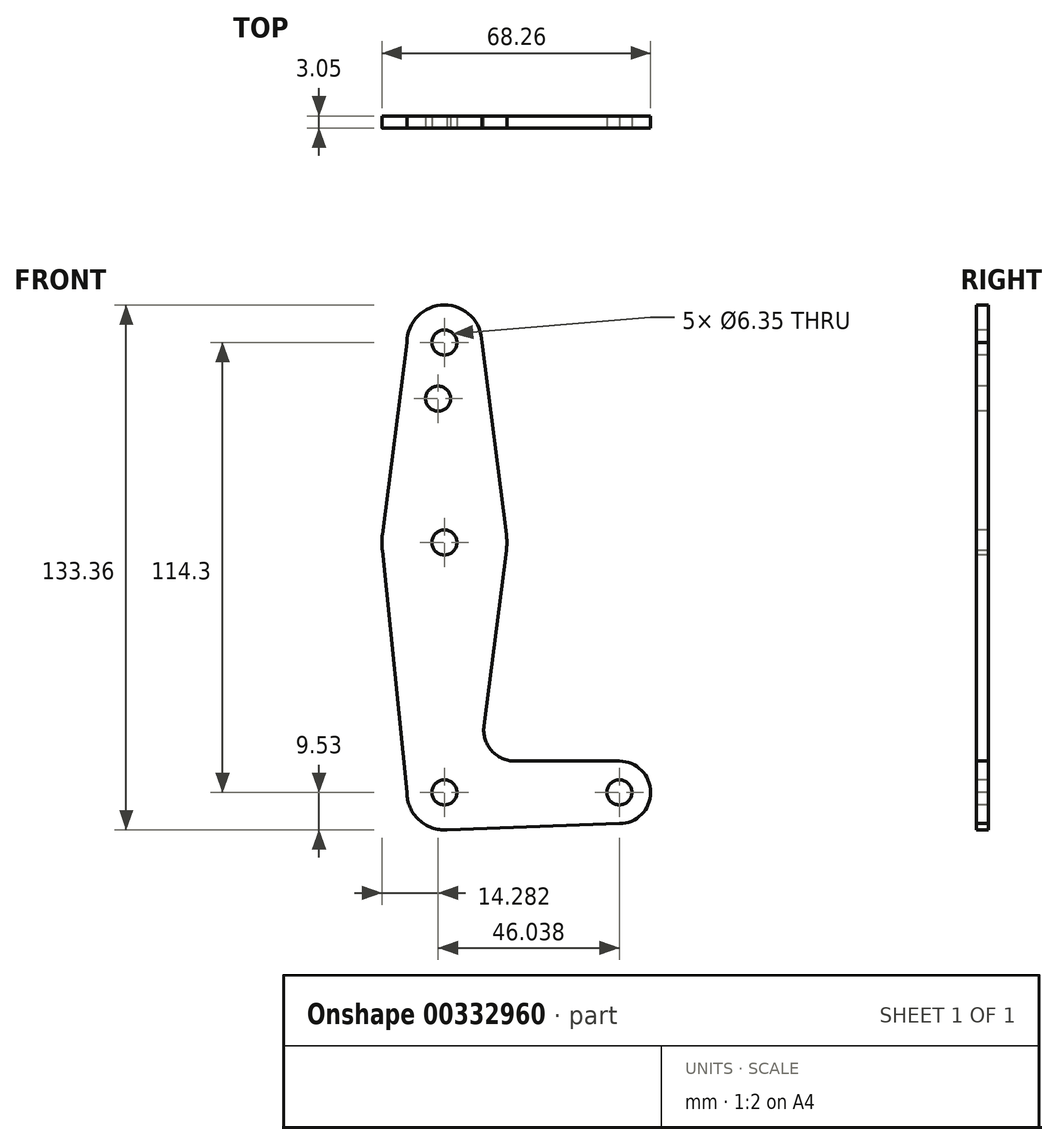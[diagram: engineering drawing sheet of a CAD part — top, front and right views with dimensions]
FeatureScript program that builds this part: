
annotation { "Feature Type Name" : "Feature", "Feature Type Description" : "" }
export const myFeature = defineFeature(function(context is Context, id is Id, definition is map)
    precondition{}
    {
        {
            var Q0;
            Q0=qCreatedBy(makeId("Front.planeOp"),FACE);
            var sketch = newSketch(context, id + "F0", { "sketchPlane" : qUnion([Q0])});
            skCircle(sketch, "E0", {"center": v(0, 0) * mm, "radius": 9.53 * mm});
            skLineSegment(sketch, "E1", {"start": v(0, 0) * mm, "end": v(44.45, 0) * mm, "construction": true});
            skCircle(sketch, "E2", {"center": v(44.45, 0) * mm, "radius": 7.94 * mm});
            skLineSegment(sketch, "E3", {"start": v(0, 0) * mm, "end": v(0, 114.3) * mm, "construction": true});
            skCircle(sketch, "E4", {"center": v(0, 63.5) * mm, "radius": 15.88 * mm});
            skCircle(sketch, "E5", {"center": v(0, 114.3) * mm, "radius": 9.53 * mm});
            skCircle(sketch, "E6", {"center": v(0, 114.3) * mm, "radius": 3.18 * mm});
            skCircle(sketch, "E7", {"center": v(0, 63.5) * mm, "radius": 3.18 * mm});
            skCircle(sketch, "E8", {"center": v(0, 0) * mm, "radius": 3.18 * mm});
            skCircle(sketch, "E9", {"center": v(44.45, 0) * mm, "radius": 3.18 * mm});
            skCircle(sketch, "E10", {"center": v(-1.59, 100.03) * mm, "radius": 3.18 * mm});
            skLineSegment(sketch, "E11", {"start": v(-15.75, 65.5) * mm, "end": v(-9.52, 114.3) * mm});
            skLineSegment(sketch, "E12", {"start": v(9.53, 114.3) * mm, "end": v(15.75, 65.5) * mm});
            skLineSegment(sketch, "E13", {"start": v(10.06, 16.9) * mm, "end": v(15.75, 61.5) * mm});
            skLineSegment(sketch, "E14", {"start": v(-9.52, 0) * mm, "end": v(-15.75, 61.5) * mm});
            skLineSegment(sketch, "E15", {"start": v(17.95, 7.94) * mm, "end": v(44.45, 7.94) * mm});
            skLineSegment(sketch, "E16", {"start": v(0, -9.53) * mm, "end": v(44.45, -7.94) * mm});
            skArc(sketch, "E17.filletArc", {"start": v(10.06, 16.9) * mm, "mid": v(11.98, 10.63) * mm, "end": v(17.95, 7.94) * mm});
            skSolve(sketch);
        }
        {
            var Q0;
            Q0 = qSketchRegion(id + "F0", true);
            extrude(context, id + "F1", {"entities" : qUnion([Q0]), "oppositeDirection" : true, "depth" : 3.05 * mm});
        }
    });
